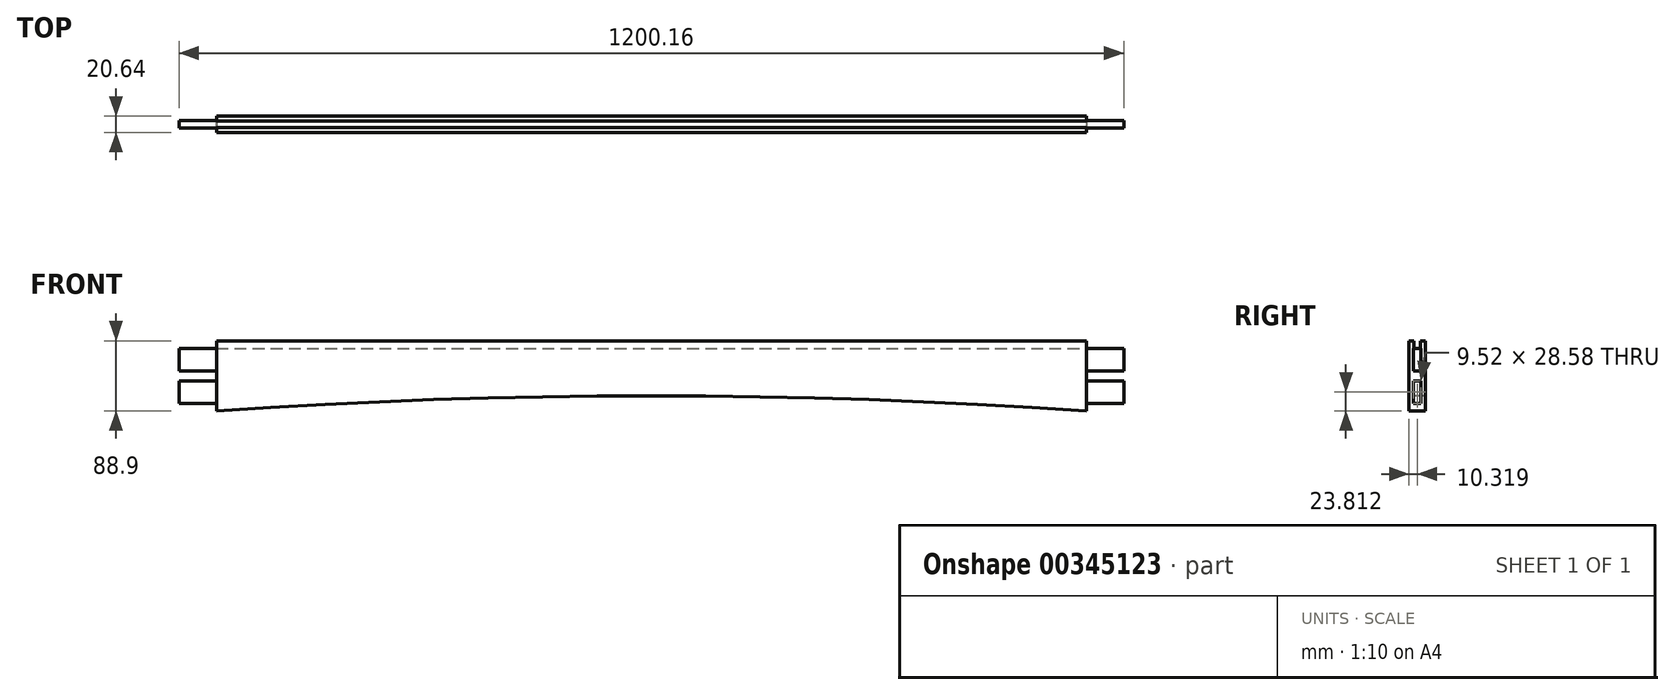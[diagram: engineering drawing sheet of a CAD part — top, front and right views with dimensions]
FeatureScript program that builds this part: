
annotation { "Feature Type Name" : "Feature", "Feature Type Description" : "" }
export const myFeature = defineFeature(function(context is Context, id is Id, definition is map)
    precondition{}
    {
        {
            var Q0;
            Q0=qCreatedBy(makeId("Front.planeOp"),FACE);
            var sketch = newSketch(context, id + "F0", { "sketchPlane" : qUnion([Q0])});
            skLineSegment(sketch, "E0", {"start": v(0, 0) * mm, "end": v(-552.45, 0) * mm});
            skLineSegment(sketch, "E1", {"start": v(0, 0) * mm, "end": v(552.45, 0) * mm});
            skLineSegment(sketch, "E2", {"start": v(-552.45, 0) * mm, "end": v(-552.45, -88.9) * mm});
            skLineSegment(sketch, "E3", {"start": v(552.45, 0) * mm, "end": v(552.45, -88.9) * mm});
            skPoint(sketch, "E4", {"position": v(0, -8089.9) * mm});
            skLineSegment(sketch, "E5", {"start": v(-199.83, -8089.9) * mm, "end": v(219.56, -8089.9) * mm, "construction": true});
            skArc(sketch, "E6", {"start": v(-552.45, -88.9) * mm, "mid": v(0, -69.85) * mm, "end": v(552.45, -88.9) * mm});
            skSolve(sketch);
        }
        {
            var Q0;
            Q0=makeQuery(id+"F0.imprint","IMPRINT",FACE,{"disambiguationData":[TD([[makeQuery(id+"F0.imprint","IMPRINT",EDGE,{"derivedFrom":sQuery(id+"F0.wireOp",EDGE,"E0")}),1.0]])]});
            extrude(context, id + "F1", {"entities" : qUnion([Q0]), "oppositeDirection" : true, "depth" : 20.64 * mm});
        }
        {
            var Q0;
            Q0=makeQuery(id+"F1.opExtrude","SWEPT_FACE",FACE,{"disambiguationData":[OSD([sQuery(id+"F0.wireOp",EDGE,"E2")])]});
            var sketch = newSketch(context, id + "F2", { "sketchPlane" : qUnion([Q0])});
            skLineSegment(sketch, "E7.bottom", {"start": v(-15.08, -38.1) * mm, "end": v(-5.56, -38.1) * mm});
            skLineSegment(sketch, "E7.top", {"start": v(-15.08, -9.52) * mm, "end": v(-5.56, -9.52) * mm});
            skLineSegment(sketch, "E7.left", {"start": v(-15.08, -38.1) * mm, "end": v(-15.08, -9.52) * mm});
            skLineSegment(sketch, "E7.right", {"start": v(-5.56, -38.1) * mm, "end": v(-5.56, -9.52) * mm});
            skPoint(sketch, "E7.middle", {"position": v(-10.32, -23.81) * mm});
            skPoint(sketch, "E7.middle.positionSnap0", {"position": v(-10.32, 0) * mm});
            skPoint(sketch, "E7.centerSnap0", {"position": v(-10.32, 0) * mm});
            skLineSegment(sketch, "E8.bottom", {"start": v(-5.56, -79.38) * mm, "end": v(-15.08, -79.38) * mm});
            skLineSegment(sketch, "E8.top", {"start": v(-5.56, -50.8) * mm, "end": v(-15.08, -50.8) * mm});
            skLineSegment(sketch, "E8.left", {"start": v(-5.56, -79.38) * mm, "end": v(-5.56, -50.8) * mm});
            skLineSegment(sketch, "E8.right", {"start": v(-15.08, -79.38) * mm, "end": v(-15.08, -50.8) * mm});
            skPoint(sketch, "E8.middle", {"position": v(-10.32, -65.09) * mm});
            skPoint(sketch, "E8.middle.positionSnap0", {"position": v(-10.32, -38.1) * mm});
            skPoint(sketch, "E8.centerSnap0", {"position": v(-10.32, -38.1) * mm});
            skSolve(sketch);
        }
        {
            var Q0;
            Q0=makeQuery(id+"F2.imprint","IMPRINT",FACE,{"disambiguationData":[TD([[makeQuery(id+"F2.imprint","IMPRINT",EDGE,{"derivedFrom":sQuery(id+"F2.wireOp",EDGE,"E7.bottom")}),1.0]])]});
            var Q1;
            Q1=makeQuery(id+"F2.imprint","IMPRINT",FACE,{"disambiguationData":[TD([[makeQuery(id+"F2.imprint","IMPRINT",EDGE,{"derivedFrom":sQuery(id+"F2.wireOp",EDGE,"E8.bottom")}),-1.0]])]});
            extrude(context, id + "F3", {"entities" : qUnion([Q0, Q1]), "operationType" : NewBodyOperationType.ADD, "depth" : 47.62 * mm});
        }
        {
            var Q0;
            Q0=makeQuery(id+"F1.opExtrude","SWEPT_FACE",FACE,{"disambiguationData":[OSD([sQuery(id+"F0.wireOp",EDGE,"E3")])]});
            var sketch = newSketch(context, id + "F4", { "sketchPlane" : qUnion([Q0])});
            skLineSegment(sketch, "E9.bottom", {"start": v(5.56, -38.1) * mm, "end": v(15.08, -38.1) * mm});
            skLineSegment(sketch, "E9.top", {"start": v(5.56, -9.53) * mm, "end": v(15.08, -9.53) * mm});
            skLineSegment(sketch, "E9.left", {"start": v(5.56, -38.1) * mm, "end": v(5.56, -9.53) * mm});
            skLineSegment(sketch, "E9.right", {"start": v(15.08, -38.1) * mm, "end": v(15.08, -9.53) * mm});
            skPoint(sketch, "E9.middle", {"position": v(10.32, -23.81) * mm});
            skPoint(sketch, "E9.middle.positionSnap0", {"position": v(10.32, 0) * mm});
            skPoint(sketch, "E9.centerSnap0", {"position": v(10.32, 0) * mm});
            skLineSegment(sketch, "E10.bottom", {"start": v(15.08, -50.8) * mm, "end": v(5.56, -50.8) * mm});
            skLineSegment(sketch, "E10.top", {"start": v(15.08, -79.38) * mm, "end": v(5.56, -79.38) * mm});
            skLineSegment(sketch, "E10.left", {"start": v(15.08, -50.8) * mm, "end": v(15.08, -79.38) * mm});
            skLineSegment(sketch, "E10.right", {"start": v(5.56, -50.8) * mm, "end": v(5.56, -79.38) * mm});
            skPoint(sketch, "E10.middle", {"position": v(10.32, -65.09) * mm});
            skPoint(sketch, "E10.middle.positionSnap0", {"position": v(10.32, -88.9) * mm});
            skPoint(sketch, "E10.centerSnap0", {"position": v(10.32, -88.9) * mm});
            skSolve(sketch);
        }
        {
            var Q0;
            Q0=makeQuery(id+"F4.imprint","IMPRINT",FACE,{"disambiguationData":[TD([[makeQuery(id+"F4.imprint","IMPRINT",EDGE,{"derivedFrom":sQuery(id+"F4.wireOp",EDGE,"E9.bottom")}),1.0]])]});
            var Q1;
            Q1=makeQuery(id+"F4.imprint","IMPRINT",FACE,{"disambiguationData":[TD([[makeQuery(id+"F4.imprint","IMPRINT",EDGE,{"derivedFrom":sQuery(id+"F4.wireOp",EDGE,"E10.bottom")}),1.0]])]});
            extrude(context, id + "F5", {"entities" : qUnion([Q0, Q1]), "operationType" : NewBodyOperationType.ADD, "depth" : 47.62 * mm});
        }
        {
            var Q0;
            Q0=makeQuery(id+"F1.opExtrude","SWEPT_FACE",FACE,{"disambiguationData":[OSD([sQuery(id+"F0.wireOp",EDGE,"E0"),sQuery(id+"F0.wireOp",EDGE,"E1")])]});
            var sketch = newSketch(context, id + "F6", { "sketchPlane" : qUnion([Q0])});
            skPoint(sketch, "E11", {"position": v(0, 10.32) * mm});
            skPoint(sketch, "E11.positionSnap0", {"position": v(0, 20.64) * mm});
            skLineSegment(sketch, "E12.bottom", {"start": v(-552.45, 6.35) * mm, "end": v(552.45, 6.35) * mm});
            skLineSegment(sketch, "E12.top", {"start": v(-552.45, 14.29) * mm, "end": v(552.45, 14.29) * mm});
            skLineSegment(sketch, "E12.left", {"start": v(-552.45, 6.35) * mm, "end": v(-552.45, 14.29) * mm});
            skLineSegment(sketch, "E12.right", {"start": v(552.45, 6.35) * mm, "end": v(552.45, 14.29) * mm});
            skSolve(sketch);
        }
        {
            var Q0;
            Q0 = qSketchRegion(id + "F6", true);
            extrude(context, id + "F7", {"entities" : qUnion([Q0]), "operationType" : NewBodyOperationType.REMOVE, "oppositeDirection" : true, "depth" : 9.52 * mm});
        }
    });
